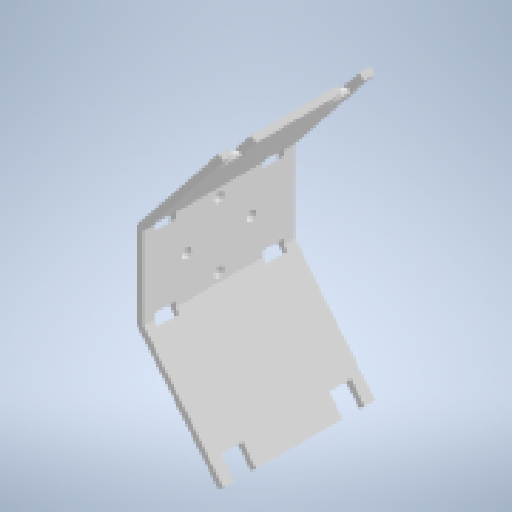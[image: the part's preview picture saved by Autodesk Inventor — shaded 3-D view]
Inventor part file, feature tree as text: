
AUTODESK INVENTOR PART (.ipt)
format: ipt  version: 2024 (Build 280153000, 153)  size: 363,008 bytes
history: native  units: in
note: dims shown in document units (in); Inventor stores cm internally (conversion verified against a paired STEP export)
features: sketch x5, extrude x4, plane x3, shell x1, fillet x1, mirror x1, hole x1
ambient origin geometry x8: Origin, YZ Plane, XZ Plane, XY Plane, X Axis, Y Axis, Z Axis, Center Point
bodies: Body1 (feature_tree)
feature tree (16):
  extrude  "Extrusion2"  Depth=1.9685in
  shell  "Shell1"  Thickness=1.9685in
  extrude  "Extrusion3"  Depth=2.7559in TaperAngle=0.0deg
  extrude  "Extrusion4"  Depth=0.1181in
  fillet  "Fillet3"  Radius=0.1181in
  plane  "Work Plane1"
  plane  "Work Plane2"
  extrude  "Extrusion5"  Depth=0.3937in
  plane  "Work Plane3"
  mirror  "Mirror1"
  hole  "Hole2"  [1 undecoded]
  sketch  "Sketch2"  dims[d4=1.5748in d5=1.9685in d6=1.9685in]
  sketch  "Sketch4"  dims[d7=1.5748in d8=2.7559in d9=0.0in]
  sketch  "Sketch5"  dims[d10=0.1181in d11=0.1181in d12=0.1181in]
  sketch  "Sketch8"  dims[d13=0.1969in d54=0.3937in]
  sketch  "Sketch9"  dims[d55=0.3937in d56=0.1969in d57=0.1969in d58=0.3937in d59=0.3937in d60=0.0in d61=0.0in d62=0.1969in d63=0.1969in d64=0.3937in d65=0.3937in d66=0.3937in d67=0.0in d68=0.0in d69=0.1181in d87=0.3937in d88=0.1969in d89=0.1575in d90=0.1969in d91=0.3937in d92=0.1575in d93=0.0in d94=0.0in d95=1.1811in d96=1.1811in d97=0.1654in d98=0.2362in d99=0.1575in d100=0.0787in d101=90.0deg d102=0.1969in d103=0.0in d14=0.0344in d15=0.0197in d16=0.0344in]
note: 1 required parameter value undecoded (feature->parameter linkage not recoverable at this tier; creation-order binding heuristic only, values carry confidence <= 0.55)
